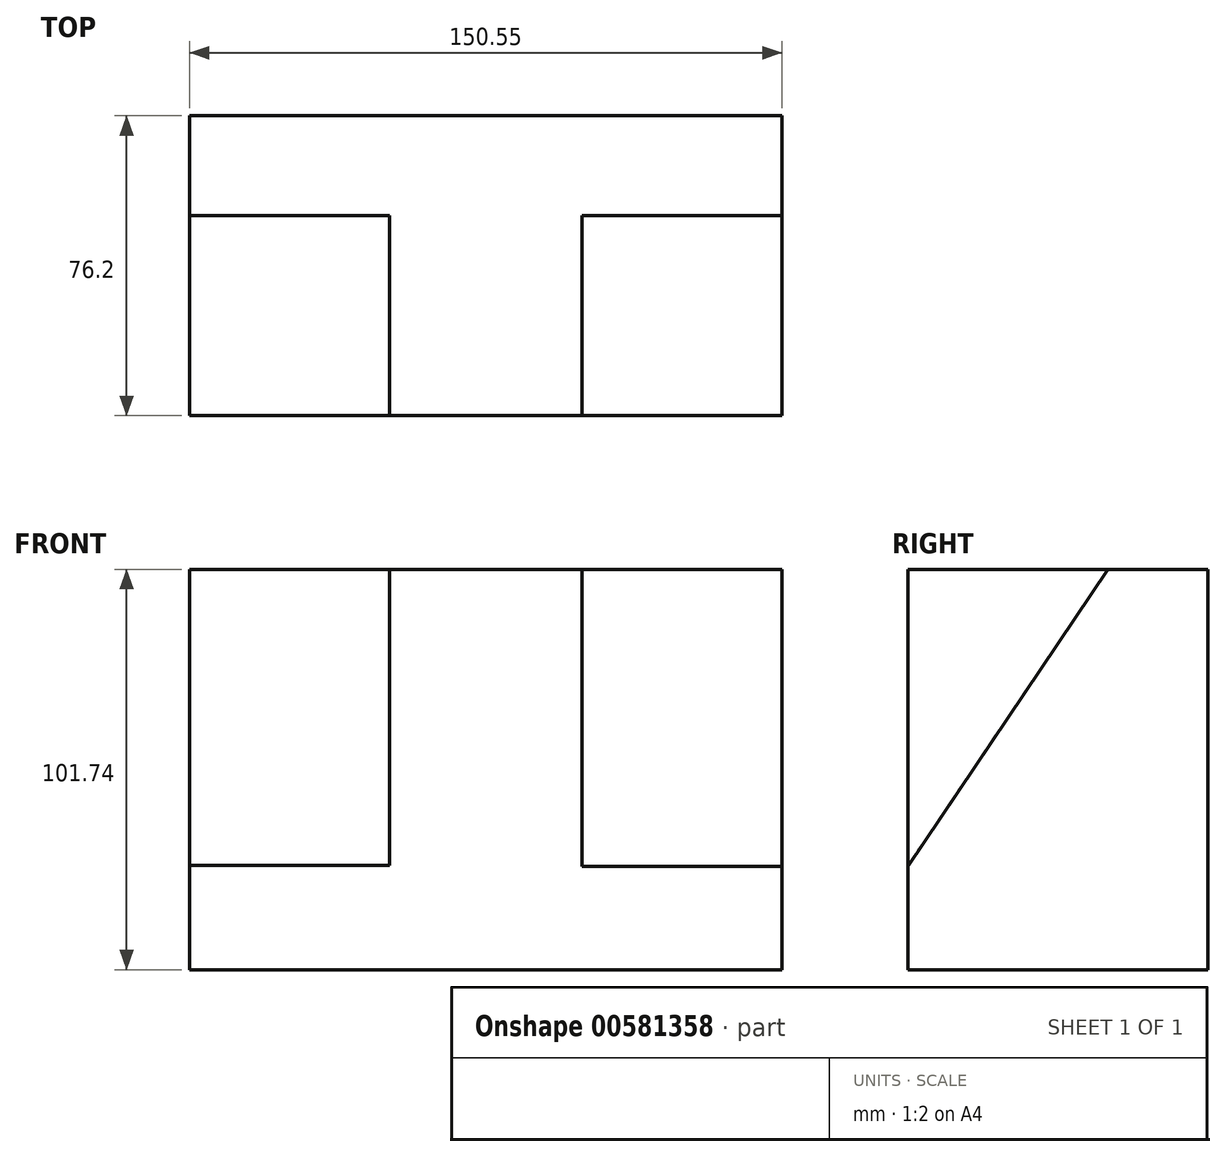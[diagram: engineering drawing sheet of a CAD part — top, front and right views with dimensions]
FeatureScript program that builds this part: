
annotation { "Feature Type Name" : "Feature", "Feature Type Description" : "" }
export const myFeature = defineFeature(function(context is Context, id is Id, definition is map)
    precondition{}
    {
        {
            var Q0;
            Q0=qCreatedBy(makeId("Front.planeOp"),FACE);
            var sketch = newSketch(context, id + "F0", { "sketchPlane" : qUnion([Q0])});
            skLineSegment(sketch, "E0.bottom", {"start": v(-76.12, 56.1) * mm, "end": v(74.43, 56.1) * mm});
            skLineSegment(sketch, "E0.top", {"start": v(-76.12, -45.65) * mm, "end": v(74.43, -45.65) * mm});
            skLineSegment(sketch, "E0.left", {"start": v(-76.12, 56.1) * mm, "end": v(-76.12, -45.65) * mm});
            skLineSegment(sketch, "E0.right", {"start": v(74.43, 56.1) * mm, "end": v(74.43, -45.65) * mm});
            skSolve(sketch);
        }
        {
            var Q0;
            Q0=makeQuery(id+"F0.imprint","IMPRINT",FACE,{"disambiguationData":[TD([[makeQuery(id+"F0.imprint","IMPRINT",EDGE,{"derivedFrom":sQuery(id+"F0.wireOp",EDGE,"E0.bottom")}),-1.0]])]});
            extrude(context, id + "F1", {"entities" : qUnion([Q0]), "depth" : 50.8 * mm, "offsetDistance" : 25.4 * mm});
        }
        {
            var Q0;
            Q0=makeQuery(id+"F1.opExtrude","SWEPT_FACE",FACE,{"disambiguationData":[OSD([sQuery(id+"F0.wireOp",EDGE,"E0.left")])]});
            var sketch = newSketch(context, id + "F2", { "sketchPlane" : qUnion([Q0])});
            skLineSegment(sketch, "E1", {"start": v(50.8, -19.18) * mm, "end": v(0, 56.1) * mm});
            skSolve(sketch);
        }
        {
            var Q0;
            {var subQ0=sQuery(id+"F2.wireOp",EDGE,"E1");Q0=makeQuery(id+"F2.imprint","IMPRINT",FACE,{"disambiguationData":[TD([[makeQuery(id+"F2.imprint","IMPRINT",EDGE,{"derivedFrom":subQ0}),-1.0]])]});}
            extrude(context, id + "F3", {"entities" : qUnion([Q0]), "operationType" : NewBodyOperationType.REMOVE, "oppositeDirection" : true, "depth" : 50.8 * mm, "offsetDistance" : 25.4 * mm});
        }
        {
            var Q0;
            Q0=makeQuery(id+"F1.opExtrude","SWEPT_FACE",FACE,{"disambiguationData":[OSD([sQuery(id+"F0.wireOp",EDGE,"E0.right")])]});
            var sketch = newSketch(context, id + "F4", { "sketchPlane" : qUnion([Q0])});
            skLineSegment(sketch, "E2", {"start": v(-50.8, -19.43) * mm, "end": v(0, 56.1) * mm});
            skSolve(sketch);
        }
        {
            var Q0;
            {var subQ0=sQuery(id+"F4.wireOp",EDGE,"E2");Q0=makeQuery(id+"F4.imprint","IMPRINT",FACE,{"disambiguationData":[TD([[makeQuery(id+"F4.imprint","IMPRINT",EDGE,{"derivedFrom":subQ0}),1.0]])]});}
            extrude(context, id + "F5", {"entities" : qUnion([Q0]), "operationType" : NewBodyOperationType.REMOVE, "oppositeDirection" : true, "depth" : 50.8 * mm, "offsetDistance" : 25.4 * mm});
        }
        {
            var Q0;
            Q0=makeQuery(id+"F1.opExtrude","CAP_FACE",FACE,{"disambiguationData":[OSD([sQuery(id+"F0.wireOp",EDGE,"E0.bottom"),sQuery(id+"F0.wireOp",EDGE,"E0.top"),sQuery(id+"F0.wireOp",EDGE,"E0.left"),sQuery(id+"F0.wireOp",EDGE,"E0.right")])],"isStart":true});
            var sketch = newSketch(context, id + "F6", { "sketchPlane" : qUnion([Q0])});
            skLineSegment(sketch, "E3.bottom", {"start": v(-74.43, 56.1) * mm, "end": v(76.12, 56.1) * mm});
            skLineSegment(sketch, "E3.top", {"start": v(-74.43, -45.65) * mm, "end": v(76.12, -45.65) * mm});
            skLineSegment(sketch, "E3.left", {"start": v(-74.43, 56.1) * mm, "end": v(-74.43, -45.65) * mm});
            skLineSegment(sketch, "E3.right", {"start": v(76.12, 56.1) * mm, "end": v(76.12, -45.65) * mm});
            skSolve(sketch);
        }
        {
            var Q0;
            Q0=makeQuery(id+"F6.imprint","IMPRINT",FACE,{"disambiguationData":[TD([[makeQuery(id+"F6.imprint","IMPRINT",EDGE,{"derivedFrom":sQuery(id+"F6.wireOp",EDGE,"E3.top")}),-1.0]])]});
            extrude(context, id + "F7", {"entities" : qUnion([Q0]), "operationType" : NewBodyOperationType.ADD, "depth" : 25.4 * mm, "offsetDistance" : 25.4 * mm});
        }
    });
